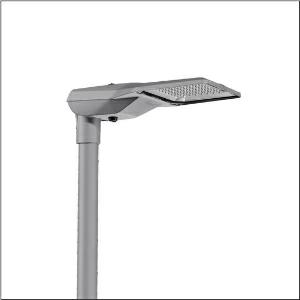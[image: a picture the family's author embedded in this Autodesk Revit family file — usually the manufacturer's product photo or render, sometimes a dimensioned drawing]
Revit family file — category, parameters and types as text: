
# Revit family: streetlight_sl_21_midi___st0_8a_5xe3c23t08lb_41e0
name_source: partatom
category: Lighting Fixtures
units: mm (PartAtom-declared; Revit-internal decimal feet)

## family parameters
Cut with Voids When Loaded = No
Host = Face
Light Source = No
Part Type = Normal
Room Calculation Point = No
Round Connector Dimension = Use Diameter
Shared = No

## types (1)
- --- (1 x LED, 11880 lm, 98.3 W, 2200K)
    Apparent Load = 98 VA
    CIE Flux Codes = 38 75 97 100 100
    Color Rendering = 70
    Color Temperature = 2200K
    Default Elevation = 1800 mm
    Description = Streetlight SL 21 midi, mast luminaire, primary light control with lens, of PMMA, primary optical cover: cover, of toughened safety glass, transparent, light distribution: ST0.8a, light emission: direct distribution, primary light characteristic: asymmetric, installation type: side-entry, post-top, LED, High Power LED, rated luminous flux: 11.880lm, luminous efficacy: 121lm/W, light colour: 722, colour temperature: 2200K, control: overheat protection, constant luminous flux control, time-dependent luminous flux control, flexible luminous flux parameterisation, presetting dimming logarithmic, mains connection: 230..240V, AC, 50/60Hz, start of lifetime: 98W, end of service life: 101W, reduction: 45W, luminaire housing, of diecast aluminium, powder-coated, Siteco® metallic grey (DB 702S), corrosivity category C5 mid according to DIN EN ISO 12944, please order mast flange separately, inclination adjustable: 0°, 5°, 10°, 15°, sealing non-destructively replaceable, multi-level sealing system, length: 644mm, width: 335mm, height: 110mm, mast flange for spigot size: 42mm (side-entry): 5XC10008XM4, 60/48mm (side-entry/post-top): 5XC10108XM2, 76/60mm (side-entry/post-top): 5XC10108XM1, Smart Interface below and above, protection rating (complete): IP66, insulation class (complete): insulation class II (safety insulation), certification: CE, ENEC, ENEC+, VDE, impact resistance: IK09, permissible operating ambient temperature for outdoor applications: -40..+50°C, standard-compliant lighting for roads and squares, packaging unit: 1 piece

Light Distribution: ST0.8a
    Height = 111 mm
    Lamp = 1 x LED
    Lamp Light Flux = 11880 lm
    Lamp Power = 98.3 W
    Lamp count = 1
    Length = 644 mm
    Luminous efficacy = 121 lm/W
    Manufacturer = Siteco
    ModVariant = No
    Model = 5XE3C23T08LB
    Number of Poles = 1
    OnlyDefault = Yes
    Power Factor = 1
    Product Name = Streetlight SL 21 midi | ST0.8a
    Product group = mast luminaire | pylon top
    ProductGroupID = 6100
    Protection Class = Protection class II
    Protection Degree = IP 66
    RLX_Detail_Level = 1
    RLX_Emergency_Light_Flux = 0 lm
    RLX_Emergency_Type = 0
    RLX_Emergency_Type_DB = No
    RlxData = <blob elided: 90681 chars, md5=2f5c9c76>
    Socket = socket
    Standby Power = 0 W
    System Light Flux = 11880 lm
    System Power = 98 W
    Type Comments = factory setting: luminous flux: 100 % | dim-lin: 254 | 1020 mA
    Type Image = l_1004304.jpg
    URL = http://relux.com
    VarID = @adj_137783
    Voltage = 0 V
    Weight = 0.00 kg
    Width = 336 mm

## geometry (parser evidence)
native form markers: Blend x4, Sweep x11
no freeform markers — native parametric forms only
